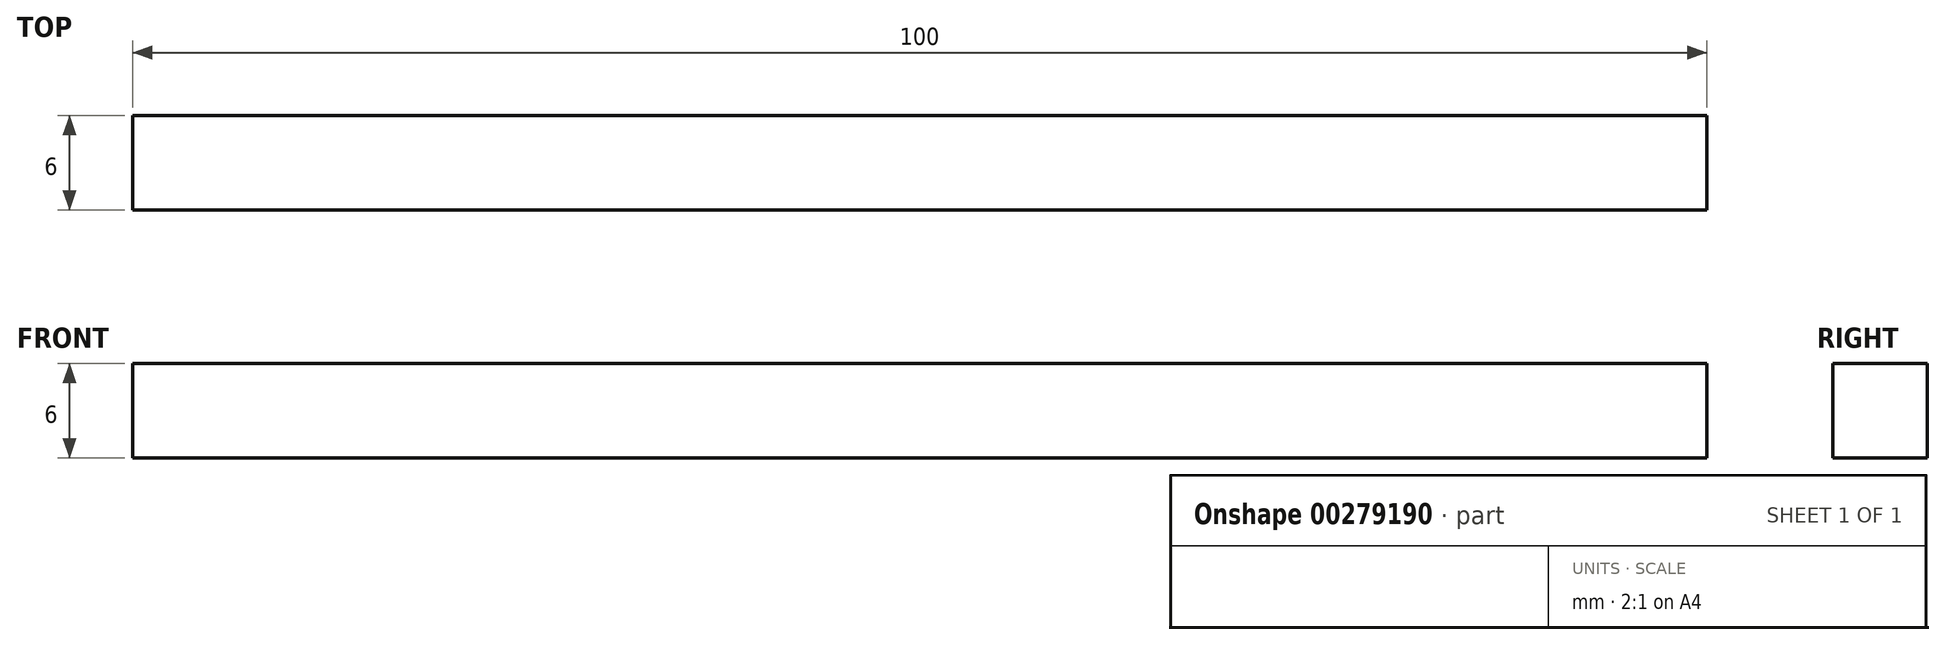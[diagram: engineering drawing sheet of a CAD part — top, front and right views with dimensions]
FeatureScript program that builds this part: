
annotation { "Feature Type Name" : "Feature", "Feature Type Description" : "" }
export const myFeature = defineFeature(function(context is Context, id is Id, definition is map)
    precondition{}
    {
        {
            var Q0;
            Q0=qCreatedBy(makeId("Front.planeOp"),FACE);
            var sketch = newSketch(context, id + "F0", { "sketchPlane" : qUnion([Q0])});
            skLineSegment(sketch, "E0", {"start": v(0, 3) * mm, "end": v(20, 3) * mm});
            skLineSegment(sketch, "E1", {"start": v(20, 3) * mm, "end": v(20, 3) * mm});
            skLineSegment(sketch, "E2", {"start": v(20, 3) * mm, "end": v(50, 3) * mm});
            skLineSegment(sketch, "E3", {"start": v(50, 3) * mm, "end": v(50, 0) * mm});
            skLineSegment(sketch, "E4.MirrorCS", {"start": v(0, -3) * mm, "end": v(20, -3) * mm});
            skLineSegment(sketch, "E5.MirrorCS", {"start": v(50, -3) * mm, "end": v(50, 0) * mm});
            skLineSegment(sketch, "E6.MirrorCS", {"start": v(20, -3) * mm, "end": v(50, -3) * mm});
            skLineSegment(sketch, "E7.MirrorCS", {"start": v(20, -3) * mm, "end": v(20, -3) * mm});
            skLineSegment(sketch, "E8.MirrorCS", {"start": v(-20, -3) * mm, "end": v(-20, -3) * mm});
            skLineSegment(sketch, "E9.MirrorCS", {"start": v(-20, -3) * mm, "end": v(-50, -3) * mm});
            skLineSegment(sketch, "E10.MirrorCS", {"start": v(-20, 3) * mm, "end": v(-20, 3) * mm});
            skLineSegment(sketch, "E11.MirrorCS", {"start": v(-20, 3) * mm, "end": v(-50, 3) * mm});
            skLineSegment(sketch, "E12.MirrorCS", {"start": v(-50, -3) * mm, "end": v(-50, 0) * mm});
            skLineSegment(sketch, "E13.MirrorCS", {"start": v(0, -3) * mm, "end": v(-20, -3) * mm});
            skLineSegment(sketch, "E14.MirrorCS", {"start": v(-50, 3) * mm, "end": v(-50, 0) * mm});
            skLineSegment(sketch, "E15.MirrorCS", {"start": v(0, 3) * mm, "end": v(-20, 3) * mm});
            skSolve(sketch);
        }
        {
            var Q0;
            Q0=qSketchRegion(id+"F0",true);
            extrude(context, id + "F1", {"entities" : qUnion([Q0]), "endBound" : BoundingType.SYMMETRIC, "depth" : 6 * mm});
        }
    });
